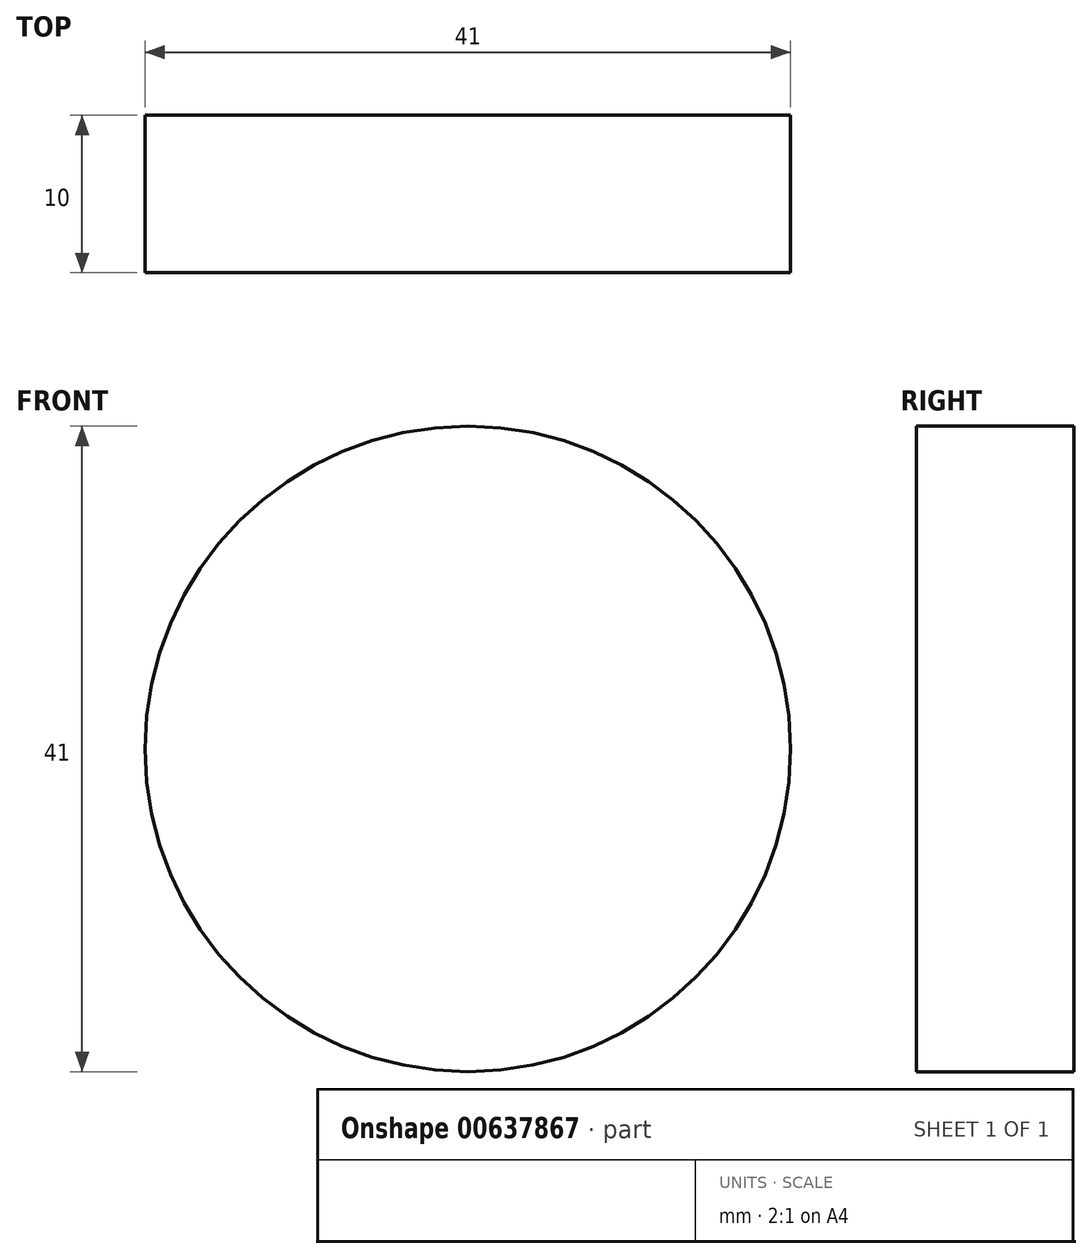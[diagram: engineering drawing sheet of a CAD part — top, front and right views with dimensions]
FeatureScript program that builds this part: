
annotation { "Feature Type Name" : "Feature", "Feature Type Description" : "" }
export const myFeature = defineFeature(function(context is Context, id is Id, definition is map)
    precondition{}
    {
        {
            var Q0;
            Q0=qCreatedBy(makeId("Front.planeOp"),FACE);
            var sketch = newSketch(context, id + "F0", { "sketchPlane" : qUnion([Q0])});
            skCircle(sketch, "E0", {"center": v(0, 0) * mm, "radius": 20.5 * mm});
            skSolve(sketch);
        }
        {
            var Q0;
            Q0 = qSketchRegion(id + "F0", true);
            extrude(context, id + "F1", {"entities" : qUnion([Q0]), "depth" : 10 * mm, "offsetDistance" : 25 * mm});
        }
    });
